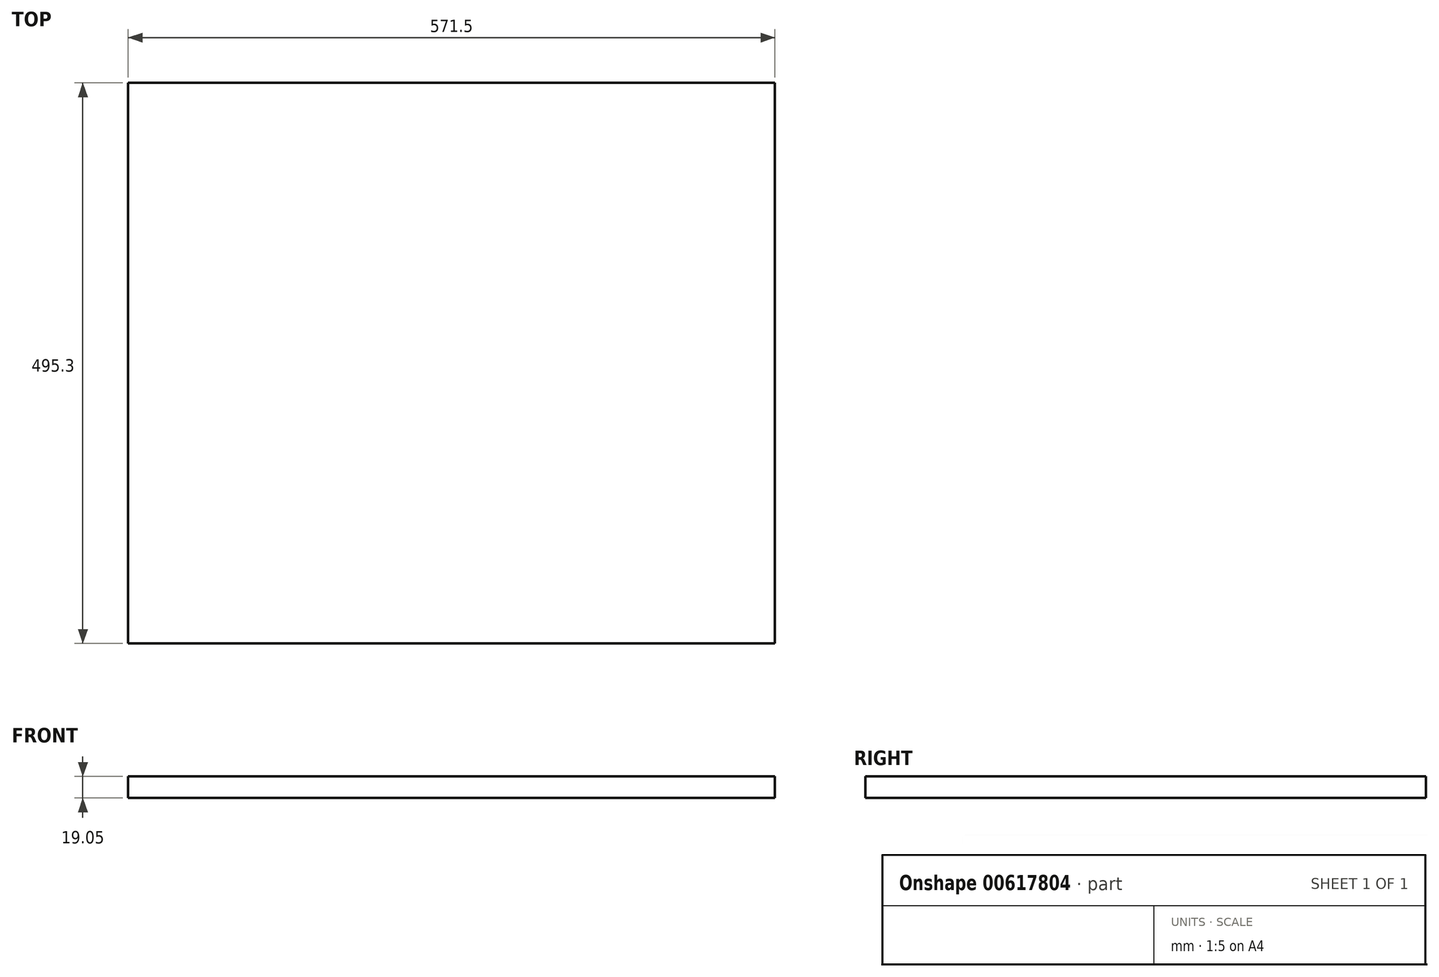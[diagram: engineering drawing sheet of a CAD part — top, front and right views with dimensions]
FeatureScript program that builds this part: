
annotation { "Feature Type Name" : "Feature", "Feature Type Description" : "" }
export const myFeature = defineFeature(function(context is Context, id is Id, definition is map)
    precondition{}
    {
        {
            var Q0;
            Q0=qCreatedBy(makeId("Top.planeOp"),FACE);
            var sketch = newSketch(context, id + "F0", { "sketchPlane" : qUnion([Q0])});
            skLineSegment(sketch, "E0.bottom", {"start": v(285.75, 247.65) * mm, "end": v(-285.75, 247.65) * mm});
            skLineSegment(sketch, "E0.top", {"start": v(285.75, -247.65) * mm, "end": v(-285.75, -247.65) * mm});
            skLineSegment(sketch, "E0.left", {"start": v(285.75, 247.65) * mm, "end": v(285.75, -247.65) * mm});
            skLineSegment(sketch, "E0.right", {"start": v(-285.75, 247.65) * mm, "end": v(-285.75, -247.65) * mm});
            skPoint(sketch, "E0.middle", {"position": v(0, 0) * mm});
            skSolve(sketch);
        }
        {
            var Q0;
            Q0=makeQuery(id+"F0.imprint","IMPRINT",FACE,{"disambiguationData":[TD([[makeQuery(id+"F0.imprint","IMPRINT",EDGE,{"derivedFrom":sQuery(id+"F0.wireOp",EDGE,"E0.bottom")}),1.0]])]});
            extrude(context, id + "F1", {"entities" : qUnion([Q0]), "depth" : 19.05 * mm, "offsetDistance" : 25.4 * mm});
        }
    });
